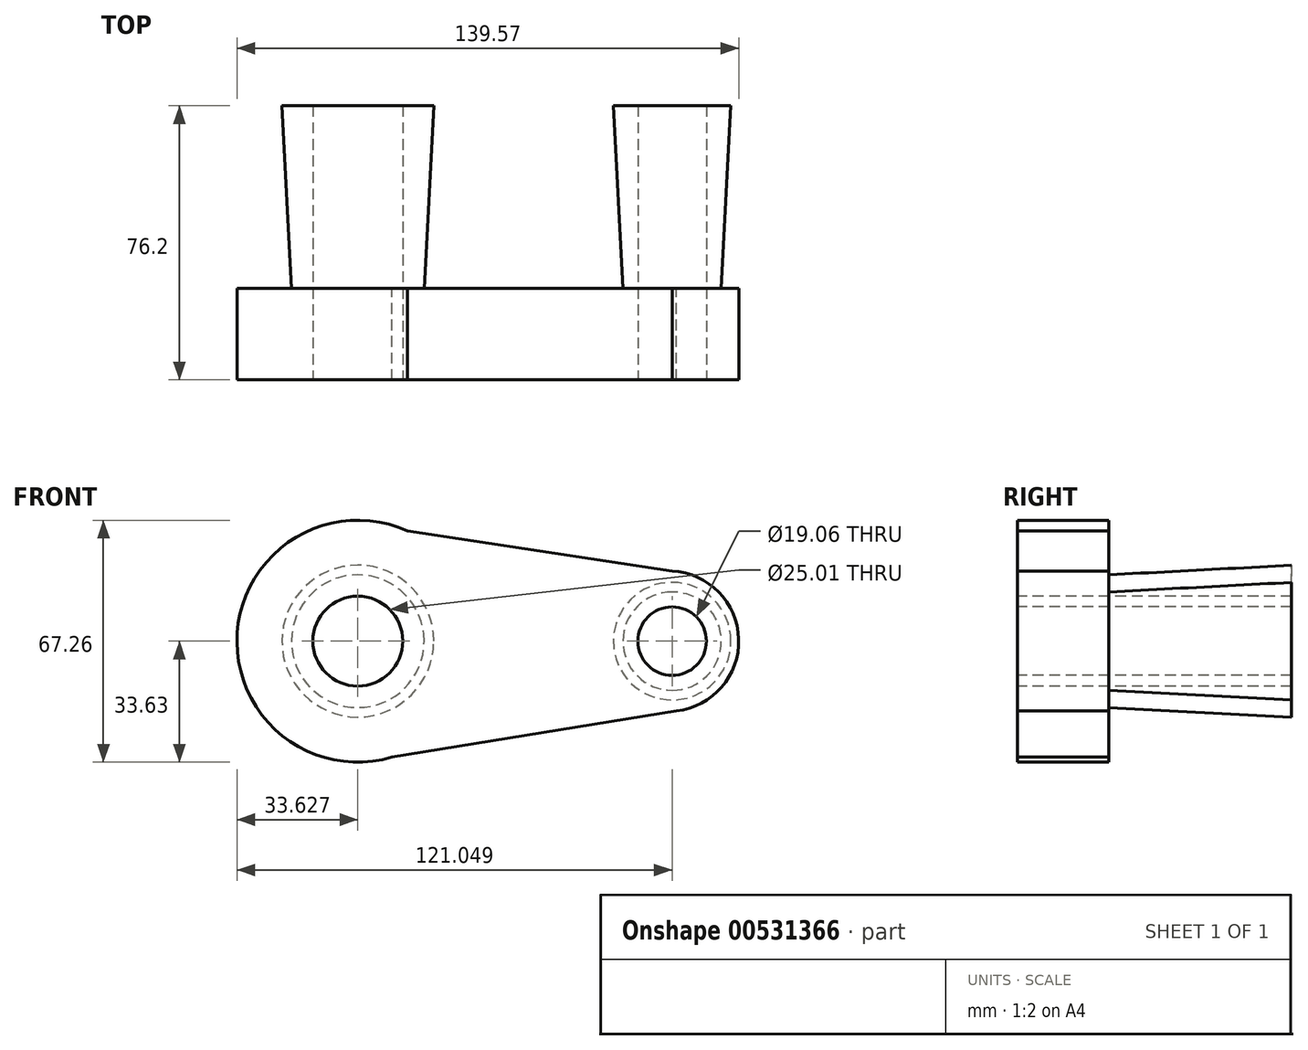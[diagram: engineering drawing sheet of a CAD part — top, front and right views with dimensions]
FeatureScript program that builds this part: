
annotation { "Feature Type Name" : "Feature", "Feature Type Description" : "" }
export const myFeature = defineFeature(function(context is Context, id is Id, definition is map)
    precondition{}
    {
        {
            var Q0;
            Q0=qCreatedBy(makeId("Front.planeOp"),FACE);
            var sketch = newSketch(context, id + "F0", { "sketchPlane" : qUnion([Q0])});
            skCircle(sketch, "E0", {"center": v(43.1, 0) * mm, "radius": 19.5 * mm});
            skCircle(sketch, "E1", {"center": v(-43.34, 0) * mm, "radius": 33.63 * mm});
            skLineSegment(sketch, "E2", {"start": v(-47.46, 33.38) * mm, "end": v(44.08, 19.48) * mm});
            skLineSegment(sketch, "E3", {"start": v(45.27, -19.38) * mm, "end": v(-42.14, -33.6) * mm});
            skSolve(sketch);
        }
        {
            var Q0;
            Q0=qSketchRegion(id+"F0",true);
            extrude(context, id + "F1", {"entities" : qUnion([Q0]), "depth" : 25.4 * mm, "offsetDistance" : 25.4 * mm});
        }
        {
            var Q0;
            Q0=makeQuery(id+"F1.opExtrude","CAP_FACE",FACE,{"disambiguationData":[OSD([sQuery(id+"F0.wireOp",EDGE,"E0"),sQuery(id+"F0.wireOp",EDGE,"E1"),sQuery(id+"F0.wireOp",EDGE,"E2"),sQuery(id+"F0.wireOp",EDGE,"E3")])],"isStart":false});
            var sketch = newSketch(context, id + "F2", { "sketchPlane" : qUnion([Q0])});
            skCircle(sketch, "E4", {"center": v(-43.34, 0) * mm, "radius": 12.5 * mm});
            skCircle(sketch, "E5", {"center": v(44.08, 0) * mm, "radius": 9.53 * mm});
            skSolve(sketch);
        }
        {
            var Q0;
            Q0=qSketchRegion(id+"F2",true);
            extrude(context, id + "F3", {"entities" : qUnion([Q0]), "operationType" : NewBodyOperationType.REMOVE, "oppositeDirection" : true, "depth" : 25.4 * mm, "offsetDistance" : 25.4 * mm});
        }
        {
            var Q0;
            Q0=makeQuery(id+"F1.opExtrude","CAP_FACE",FACE,{"disambiguationData":[OSD([sQuery(id+"F0.wireOp",EDGE,"E0"),sQuery(id+"F0.wireOp",EDGE,"E1"),sQuery(id+"F0.wireOp",EDGE,"E2"),sQuery(id+"F0.wireOp",EDGE,"E3")])],"isStart":true});
            var sketch = newSketch(context, id + "F4", { "sketchPlane" : qUnion([Q0])});
            skCircle(sketch, "E6", {"center": v(43.34, 0) * mm, "radius": 18.45 * mm});
            skCircle(sketch, "E7", {"center": v(-44.08, 0) * mm, "radius": 13.68 * mm});
            skSolve(sketch);
        }
        {
            var Q0;
            Q0=qSketchRegion(id+"F4",true);
            extrude(context, id + "F5", {"entities" : qUnion([Q0]), "operationType" : NewBodyOperationType.ADD, "depth" : 50.8 * mm, "offsetDistance" : 25.4 * mm, "hasDraft" : true, "draftAngle" : 3 * degree});
        }
        {
            var Q0;
            Q0=makeQuery(id+"F5.opExtrude","CAP_FACE",FACE,{"disambiguationData":[OSD([sQuery(id+"F4.wireOp",EDGE,"E6")])],"isStart":true});
            extrude(context, id + "F6", {"entities" : qUnion([Q0]), "operationType" : NewBodyOperationType.REMOVE, "oppositeDirection" : true, "depth" : 50.8 * mm, "offsetDistance" : 25.4 * mm});
        }
        {
            var Q0;
            Q0=makeQuery(id+"F5.opExtrude","CAP_FACE",FACE,{"disambiguationData":[OSD([sQuery(id+"F4.wireOp",EDGE,"E7")])],"isStart":true});
            extrude(context, id + "F7", {"entities" : qUnion([Q0]), "operationType" : NewBodyOperationType.REMOVE, "oppositeDirection" : true, "depth" : 50.8 * mm, "offsetDistance" : 25.4 * mm});
        }
    });
